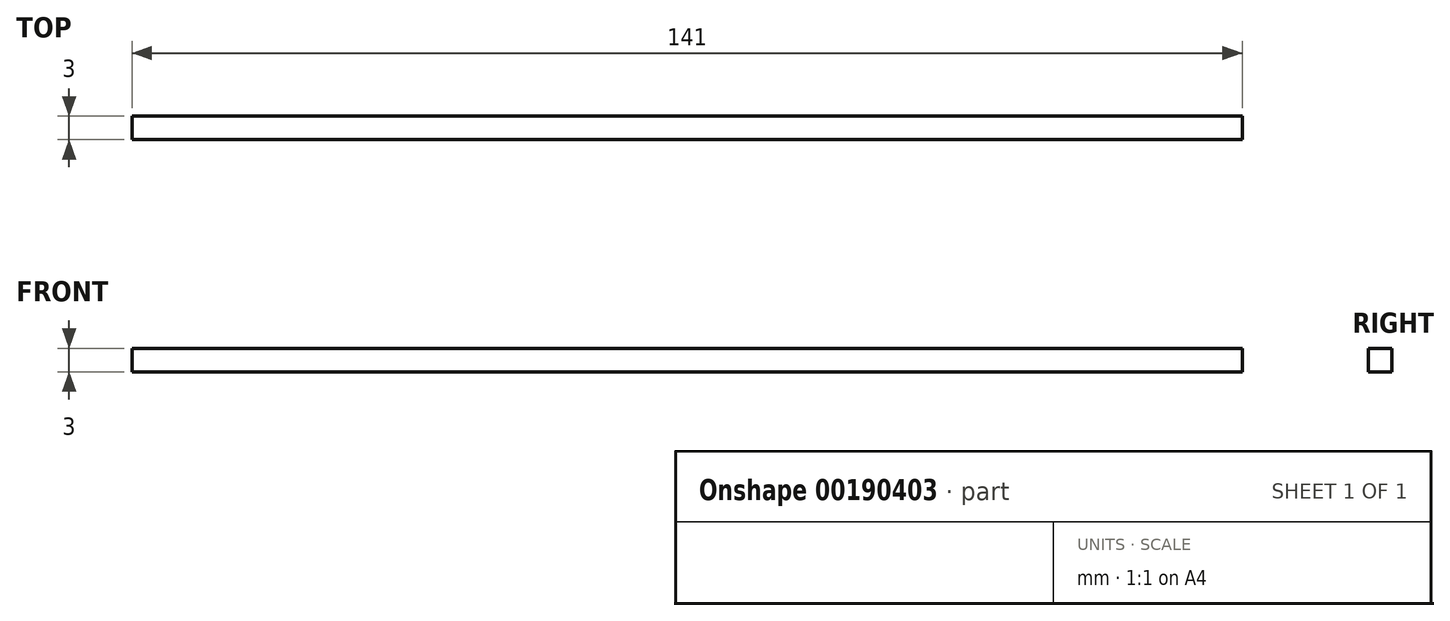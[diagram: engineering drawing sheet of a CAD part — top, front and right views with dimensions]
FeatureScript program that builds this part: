
annotation { "Feature Type Name" : "Feature", "Feature Type Description" : "" }
export const myFeature = defineFeature(function(context is Context, id is Id, definition is map)
    precondition{}
    {
        {
            var Q0;
            Q0=qCreatedBy(makeId("Top.planeOp"),FACE);
            var sketch = newSketch(context, id + "F0", { "sketchPlane" : qUnion([Q0])});
            skLineSegment(sketch, "E0.bottom", {"start": v(0, 0) * mm, "end": v(120, 0) * mm});
            skLineSegment(sketch, "E0.top", {"start": v(0, 200) * mm, "end": v(120, 200) * mm});
            skLineSegment(sketch, "E0.left", {"start": v(0, 0) * mm, "end": v(0, 200) * mm});
            skLineSegment(sketch, "E0.right", {"start": v(120, 0) * mm, "end": v(120, 200) * mm});
            skLineSegment(sketch, "E1", {"start": v(47, 118) * mm, "end": v(73, 118) * mm});
            skLineSegment(sketch, "E2", {"start": v(73, 118) * mm, "end": v(120, 0) * mm});
            skLineSegment(sketch, "E3", {"start": v(47, 118) * mm, "end": v(0, 0) * mm});
            skLineSegment(sketch, "E4", {"start": v(92.12, 70) * mm, "end": v(120, 70) * mm});
            skLineSegment(sketch, "E5", {"start": v(120, 200) * mm, "end": v(74, 200) * mm});
            skLineSegment(sketch, "E6", {"start": v(74, 200) * mm, "end": v(74, 140) * mm});
            skLineSegment(sketch, "E7", {"start": v(74, 140) * mm, "end": v(92.89, 129.96) * mm});
            skLineSegment(sketch, "E8", {"start": v(92.89, 129.96) * mm, "end": v(92.12, 70) * mm});
            skLineSegment(sketch, "E9", {"start": v(0, 95) * mm, "end": v(35, 95) * mm});
            skLineSegment(sketch, "E10", {"start": v(35, 95) * mm, "end": v(35, 200) * mm});
            skSolve(sketch);
        }
        {
            var Q0;
            Q0=qCreatedBy(makeId("Top.planeOp"),FACE);
            var sketch = newSketch(context, id + "F1", { "sketchPlane" : qUnion([Q0])});
            skLineSegment(sketch, "E11.bottom", {"start": v(-145.63, -46.02) * mm, "end": v(-4.63, -46.02) * mm});
            skLineSegment(sketch, "E11.top", {"start": v(-145.63, -49.02) * mm, "end": v(-4.63, -49.02) * mm});
            skLineSegment(sketch, "E11.left", {"start": v(-145.63, -46.02) * mm, "end": v(-145.63, -49.02) * mm});
            skLineSegment(sketch, "E11.right", {"start": v(-4.63, -46.02) * mm, "end": v(-4.63, -49.02) * mm});
            skSolve(sketch);
        }
        {
            var Q0;
            Q0=makeQuery(id+"F1.imprint","IMPRINT",FACE,{"disambiguationData":[TD([[makeQuery(id+"F1.imprint","IMPRINT",EDGE,{"derivedFrom":sQuery(id+"F1.wireOp",EDGE,"E11.bottom")}),-1.0]])]});
            extrude(context, id + "F2", {"entities" : qUnion([Q0]), "depth" : 3 * mm, "offsetDistance" : 25 * mm});
        }
    });
